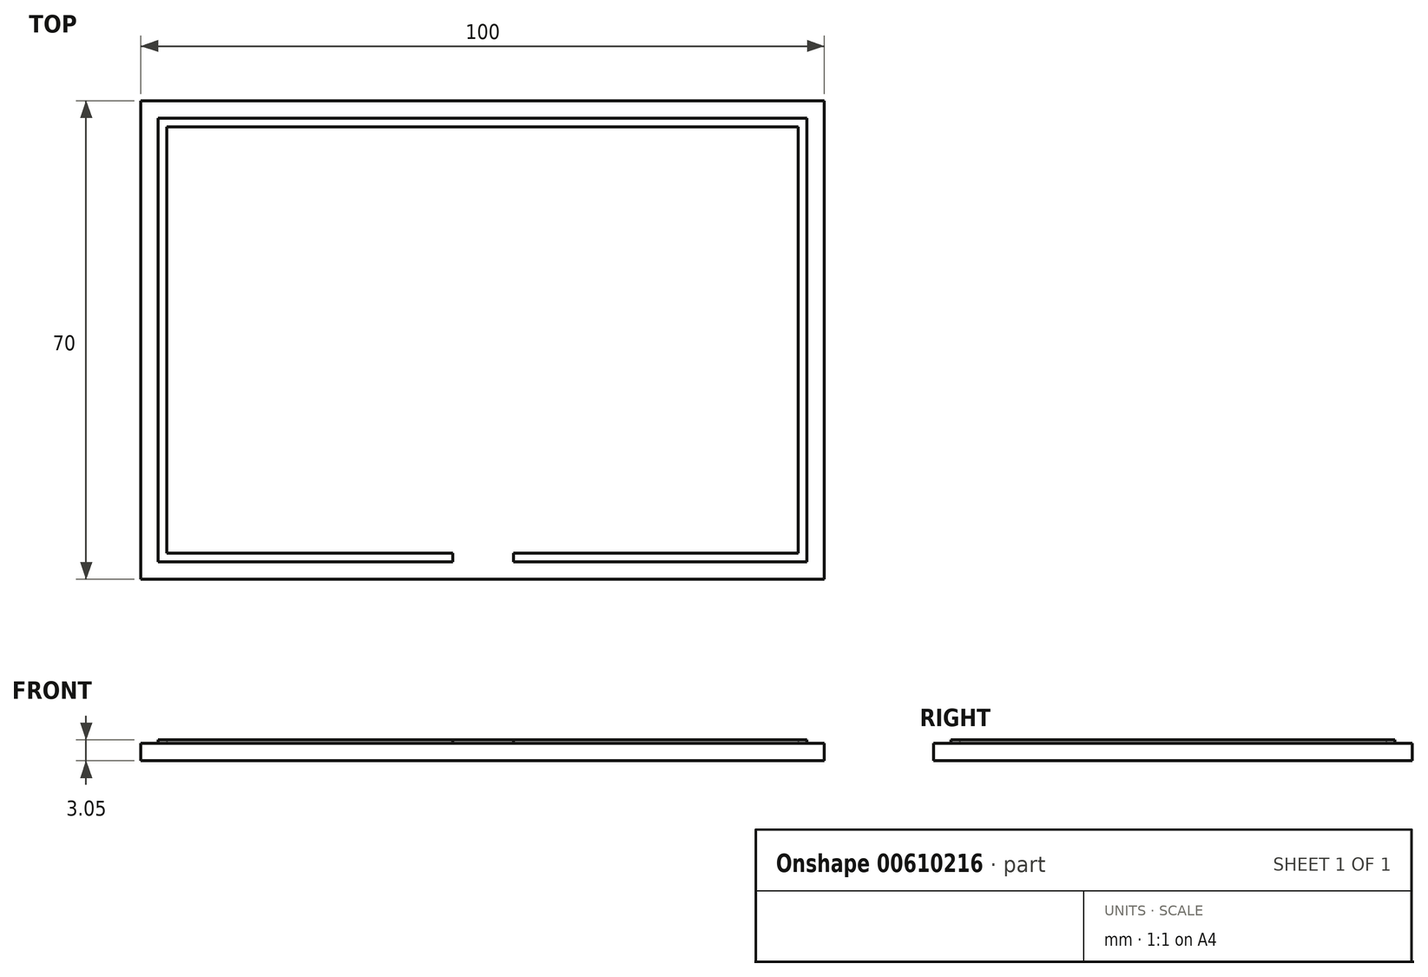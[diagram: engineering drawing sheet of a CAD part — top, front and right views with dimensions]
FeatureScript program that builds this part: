
annotation { "Feature Type Name" : "Feature", "Feature Type Description" : "" }
export const myFeature = defineFeature(function(context is Context, id is Id, definition is map)
    precondition{}
    {
        {
            var Q0;
            Q0=qCreatedBy(makeId("Top.planeOp"),FACE);
            var sketch = newSketch(context, id + "F0", { "sketchPlane" : qUnion([Q0])});
            skLineSegment(sketch, "E0.bottom", {"start": v(-50, 35) * mm, "end": v(50, 35) * mm});
            skLineSegment(sketch, "E0.top", {"start": v(-50, -35) * mm, "end": v(50, -35) * mm});
            skLineSegment(sketch, "E0.left", {"start": v(-50, 35) * mm, "end": v(-50, -35) * mm});
            skLineSegment(sketch, "E0.right", {"start": v(50, 35) * mm, "end": v(50, -35) * mm});
            skPoint(sketch, "E0.middle", {"position": v(0, 0) * mm});
            skSolve(sketch);
        }
        {
            var Q0;
            Q0 = qSketchRegion(id + "F0", true);
            extrude(context, id + "F1", {"entities" : qUnion([Q0]), "depth" : 2.54 * mm, "offsetDistance" : 25.4 * mm});
        }
        {
            var Q0;
            Q0=makeQuery(id+"F1.opExtrude","CAP_FACE",FACE,{"disambiguationData":[OSD([sQuery(id+"F0.wireOp",EDGE,"E0.bottom"),sQuery(id+"F0.wireOp",EDGE,"E0.top"),sQuery(id+"F0.wireOp",EDGE,"E0.left"),sQuery(id+"F0.wireOp",EDGE,"E0.right")])],"isStart":false});
            var sketch = newSketch(context, id + "F2", { "sketchPlane" : qUnion([Q0])});
            skLineSegment(sketch, "E1.0", {"start": v(-46.19, 31.19) * mm, "end": v(-46.2, -31.2) * mm});
            skLineSegment(sketch, "E1.1", {"start": v(46.2, 31.2) * mm, "end": v(-46.19, 31.2) * mm});
            skLineSegment(sketch, "E1.2", {"start": v(46.19, -31.2) * mm, "end": v(46.2, 31.2) * mm});
            skLineSegment(sketch, "E1.3", {"start": v(-46.2, -31.2) * mm, "end": v(46.19, -31.2) * mm});
            skLineSegment(sketch, "E2.0", {"start": v(47.46, 32.46) * mm, "end": v(-47.46, 32.46) * mm});
            skLineSegment(sketch, "E2.1", {"start": v(47.46, -32.46) * mm, "end": v(47.46, 32.46) * mm});
            skLineSegment(sketch, "E2.2", {"start": v(-47.46, -32.46) * mm, "end": v(47.46, -32.46) * mm});
            skLineSegment(sketch, "E2.3", {"start": v(-47.46, 32.46) * mm, "end": v(-47.46, -32.46) * mm});
            skSolve(sketch);
        }
        {
            var Q0;
            Q0=makeQuery(id+"F2.imprint","IMPRINT",FACE,{"disambiguationData":[TD([[makeQuery(id+"F2.imprint","IMPRINT",EDGE,{"derivedFrom":sQuery(id+"F2.wireOp",EDGE,"E1.0")}),-1.0]])]});
            extrude(context, id + "F3", {"entities" : qUnion([Q0]), "operationType" : NewBodyOperationType.ADD, "depth" : 0.5 * mm, "offsetDistance" : 25.4 * mm});
        }
        {
            var Q0;
            Q0=makeQuery(id+"F3.opExtrude","SWEPT_FACE",FACE,{"disambiguationData":[OSD([sQuery(id+"F2.wireOp",EDGE,"E2.2")])]});
            var sketch = newSketch(context, id + "F4", { "sketchPlane" : qUnion([Q0])});
            skLineSegment(sketch, "E3.bottom", {"start": v(-4.36, 2.54) * mm, "end": v(4.5, 2.54) * mm});
            skLineSegment(sketch, "E3.top", {"start": v(-4.36, 3.05) * mm, "end": v(4.5, 3.05) * mm});
            skLineSegment(sketch, "E3.left", {"start": v(-4.36, 2.54) * mm, "end": v(-4.36, 3.05) * mm});
            skLineSegment(sketch, "E3.right", {"start": v(4.5, 2.54) * mm, "end": v(4.5, 3.05) * mm});
            skSolve(sketch);
        }
        {
            var Q0;
            Q0 = qSketchRegion(id + "F4", true);
            extrude(context, id + "F5", {"entities" : qUnion([Q0]), "operationType" : NewBodyOperationType.REMOVE, "oppositeDirection" : true, "depth" : 25.4 * mm, "offsetDistance" : 25.4 * mm});
        }
    });
